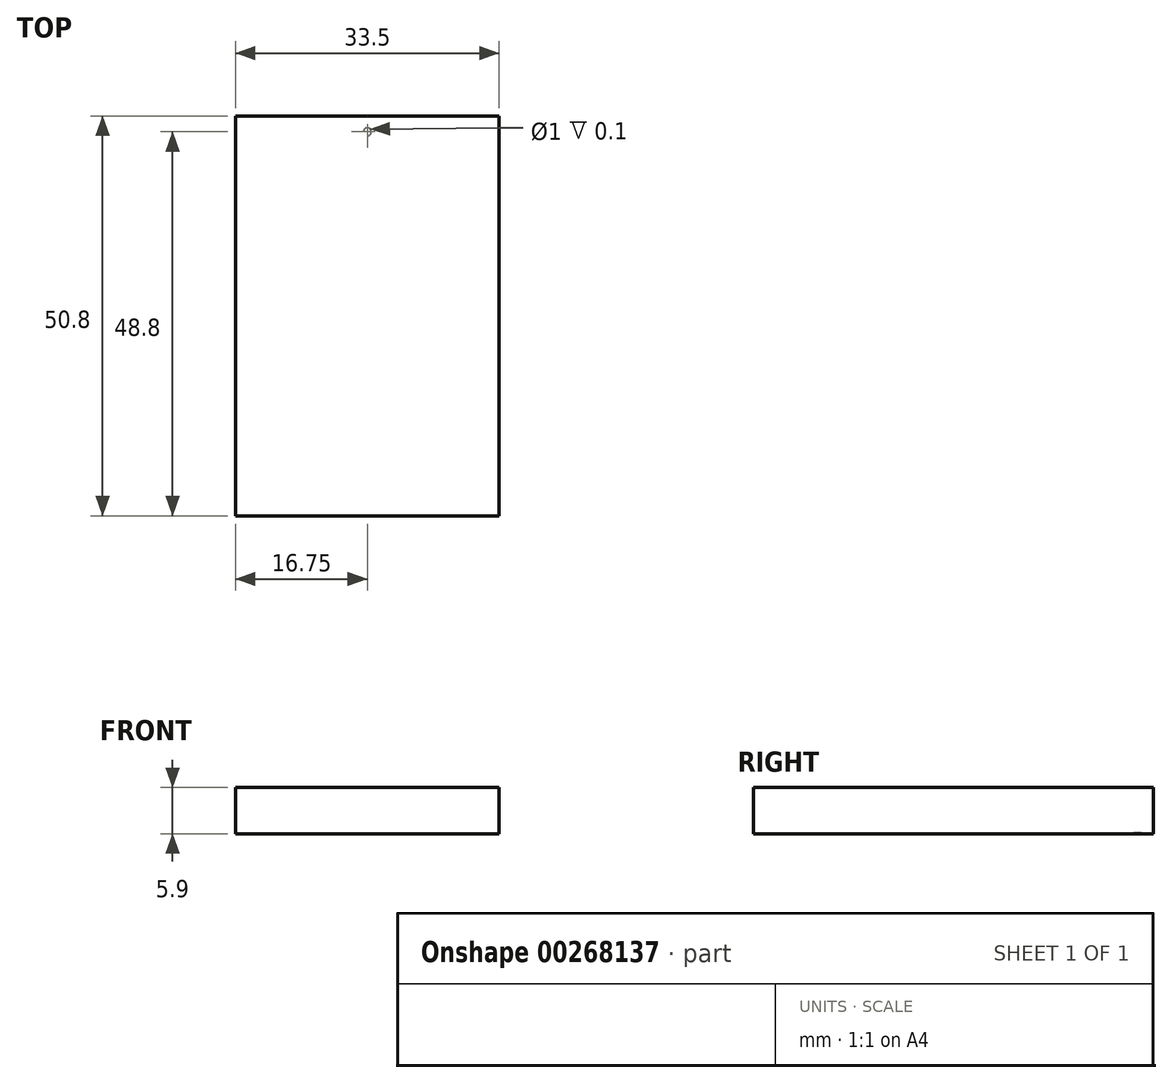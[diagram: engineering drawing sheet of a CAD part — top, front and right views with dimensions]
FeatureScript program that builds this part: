
annotation { "Feature Type Name" : "Feature", "Feature Type Description" : "" }
export const myFeature = defineFeature(function(context is Context, id is Id, definition is map)
    precondition{}
    {
        {
            var Q0;
            Q0=qCreatedBy(makeId("Top.planeOp"),FACE);
            var sketch = newSketch(context, id + "F0", { "sketchPlane" : qUnion([Q0])});
            skLineSegment(sketch, "E0.bottom", {"start": v(-16.75, 25.4) * mm, "end": v(16.75, 25.4) * mm});
            skLineSegment(sketch, "E0.top", {"start": v(-16.75, -25.4) * mm, "end": v(16.75, -25.4) * mm});
            skLineSegment(sketch, "E0.left", {"start": v(-16.75, 25.4) * mm, "end": v(-16.75, -25.4) * mm});
            skLineSegment(sketch, "E0.right", {"start": v(16.75, 25.4) * mm, "end": v(16.75, -25.4) * mm});
            skPoint(sketch, "E0.middle", {"position": v(0, 0) * mm});
            skSolve(sketch);
        }
        {
            var Q0;
            Q0=makeQuery(id+"F0.imprint","IMPRINT",FACE,{"disambiguationData":[TD([[makeQuery(id+"F0.imprint","IMPRINT",EDGE,{"derivedFrom":sQuery(id+"F0.wireOp",EDGE,"E0.bottom")}),-1.0]])]});
            extrude(context, id + "F1", {"entities" : qUnion([Q0]), "depth" : 5.9 * mm, "offsetDistance" : 25 * mm});
        }
        {
            var Q0;
            Q0=makeQuery(id+"F1.opExtrude","CAP_FACE",FACE,{"disambiguationData":[OSD([sQuery(id+"F0.wireOp",EDGE,"E0.bottom"),sQuery(id+"F0.wireOp",EDGE,"E0.top"),sQuery(id+"F0.wireOp",EDGE,"E0.left"),sQuery(id+"F0.wireOp",EDGE,"E0.right")])],"isStart":true});
            var sketch = newSketch(context, id + "F2", { "sketchPlane" : qUnion([Q0])});
            skLineSegment(sketch, "E1", {"start": v(0, -25.4) * mm, "end": v(0, -23.4) * mm});
            skCircle(sketch, "E2", {"center": v(0, -23.4) * mm, "radius": 0.5 * mm});
            skSolve(sketch);
        }
        {
            var Q0;
            Q0=makeQuery(id+"F2.imprint","IMPRINT",FACE,{"disambiguationData":[TD([[makeQuery(id+"F2.imprint","IMPRINT",EDGE,{"derivedFrom":sQuery(id+"F2.wireOp",EDGE,"E2")}),1.0]])]});
            extrude(context, id + "F3", {"entities" : qUnion([Q0]), "operationType" : NewBodyOperationType.REMOVE, "oppositeDirection" : true, "depth" : 0.1 * mm, "offsetDistance" : 25 * mm});
        }
    });
